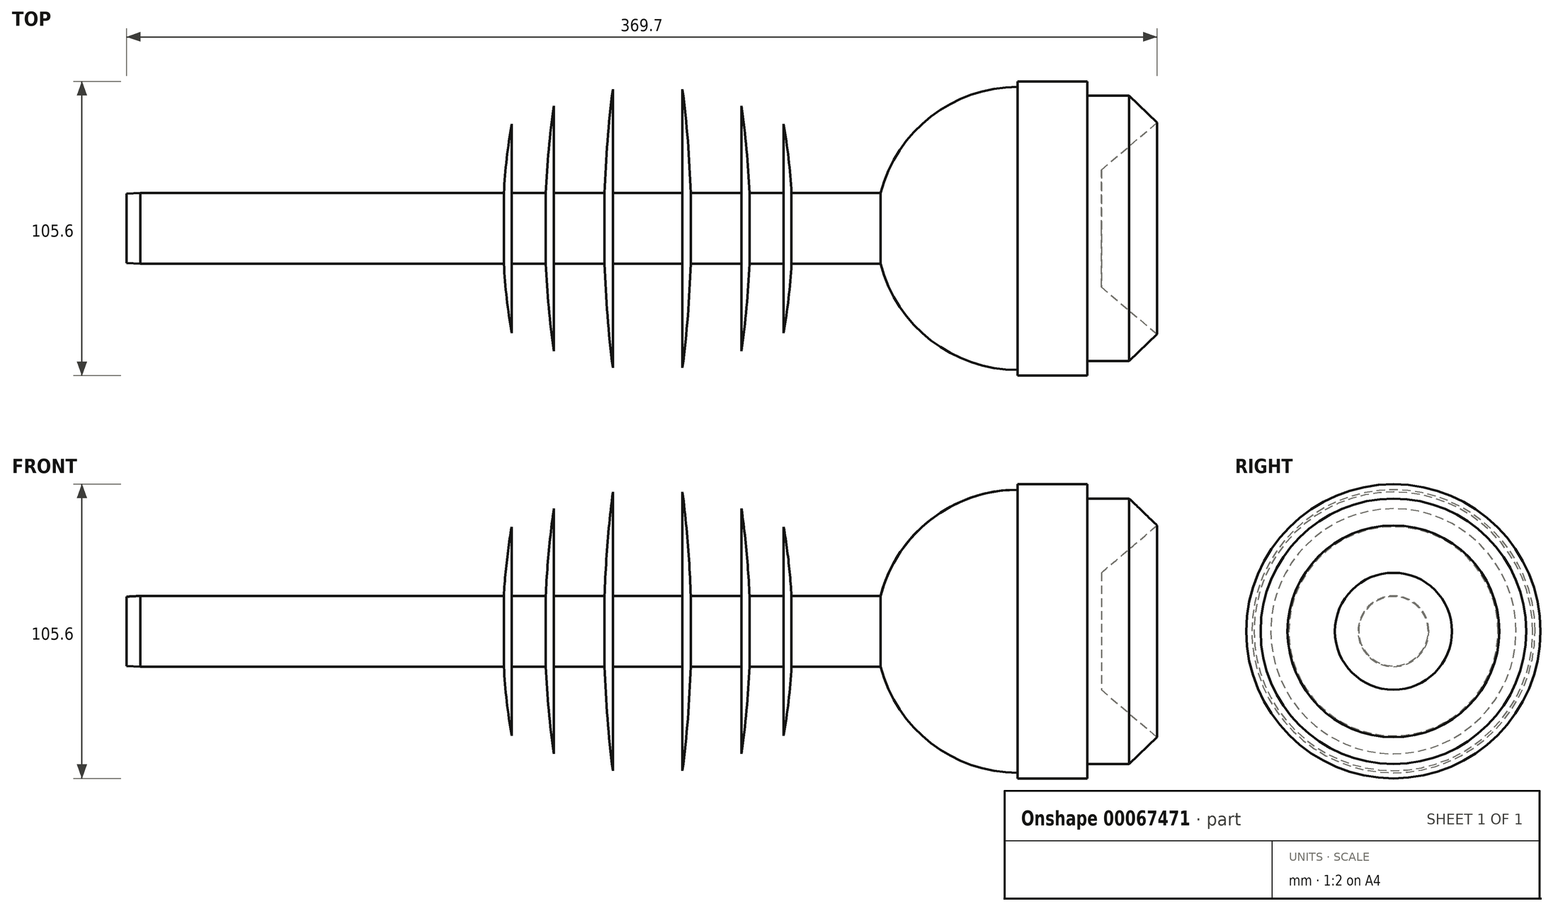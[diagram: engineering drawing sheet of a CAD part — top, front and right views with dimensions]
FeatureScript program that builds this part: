
annotation { "Feature Type Name" : "Feature", "Feature Type Description" : "" }
export const myFeature = defineFeature(function(context is Context, id is Id, definition is map)
    precondition{}
    {
        {
            assignVariable(context, id + "F0", {"name" : "s", "anyValue" : 1});
        }
        {
            var Q0;
            Q0=qCreatedBy(makeId("Top.planeOp"),FACE);
            var sketch = newSketch(context, id + "F1", { "sketchPlane" : qUnion([Q0])});
            skLineSegment(sketch, "E0", {"start": v(0, 0) * mm, "end": v(0, 12.7) * mm});
            skLineSegment(sketch, "E1", {"start": v(0, 12.7) * mm, "end": v(181.95, 12.7) * mm});
            skLineSegment(sketch, "E2", {"start": v(0, 0) * mm, "end": v(130, 0) * mm});
            skLineSegment(sketch, "E3", {"start": v(130, 0) * mm, "end": v(133.15, 0) * mm});
            skLineSegment(sketch, "E4", {"start": v(133.15, 0) * mm, "end": v(145.15, 0) * mm});
            skLineSegment(sketch, "E5", {"start": v(145.15, 0) * mm, "end": v(148.3, 0) * mm});
            skLineSegment(sketch, "E6", {"start": v(148.3, 0) * mm, "end": v(166.3, 0) * mm});
            skLineSegment(sketch, "E7", {"start": v(166.3, 0) * mm, "end": v(169.45, 0) * mm});
            skLineSegment(sketch, "E8", {"start": v(169.45, 0) * mm, "end": v(181.95, 0) * mm});
            skLineSegment(sketch, "E9", {"start": v(130, 0) * mm, "end": v(130, 12.7) * mm, "construction": true});
            skLineSegment(sketch, "E10", {"start": v(145.15, 0) * mm, "end": v(145.15, 12.7) * mm, "construction": true});
            skLineSegment(sketch, "E11", {"start": v(166.3, 0) * mm, "end": v(166.3, 12.7) * mm, "construction": true});
            skLineSegment(sketch, "E12", {"start": v(181.95, 0) * mm, "end": v(181.95, 12.7) * mm, "construction": true});
            skLineSegment(sketch, "E13", {"start": v(133.15, 12.7) * mm, "end": v(133.15, 37.5) * mm});
            skLineSegment(sketch, "E14", {"start": v(148.3, 12.7) * mm, "end": v(148.3, 44) * mm});
            skLineSegment(sketch, "E15", {"start": v(169.45, 12.7) * mm, "end": v(169.45, 50) * mm});
            skArc(sketch, "E16", {"start": v(133.15, 37.5) * mm, "mid": v(130.79, 18.82) * mm, "end": v(130, 0) * mm});
            skArc(sketch, "E17", {"start": v(148.3, 44) * mm, "mid": v(145.94, 22.06) * mm, "end": v(145.15, 0) * mm});
            skArc(sketch, "E18", {"start": v(169.45, 50) * mm, "mid": v(167.09, 25.05) * mm, "end": v(166.3, 0) * mm});
            skLineSegment(sketch, "E19.MirrorCS", {"start": v(194.45, 12.7) * mm, "end": v(194.45, 50) * mm});
            skArc(sketch, "E20.MirrorCS", {"start": v(194.45, 50) * mm, "mid": v(196.81, 25.05) * mm, "end": v(197.6, 0) * mm});
            skLineSegment(sketch, "E21.MirrorCS", {"start": v(215.6, 12.7) * mm, "end": v(215.6, 44) * mm});
            skArc(sketch, "E22.MirrorCS", {"start": v(215.6, 44) * mm, "mid": v(217.96, 22.06) * mm, "end": v(218.75, 0) * mm});
            skLineSegment(sketch, "E23.MirrorCS", {"start": v(230.75, 12.7) * mm, "end": v(230.75, 37.5) * mm});
            skArc(sketch, "E24.MirrorCS", {"start": v(230.75, 37.5) * mm, "mid": v(233.11, 18.82) * mm, "end": v(233.9, 0) * mm});
            skLineSegment(sketch, "E25", {"start": v(181.95, 0) * mm, "end": v(263.9, 0) * mm});
            skLineSegment(sketch, "E26", {"start": v(263.9, 0) * mm, "end": v(314.7, 0) * mm});
            skLineSegment(sketch, "E27", {"start": v(314.7, 0) * mm, "end": v(344.7, 0) * mm});
            skLineSegment(sketch, "E28", {"start": v(344.7, 0) * mm, "end": v(344.7, 21) * mm});
            skLineSegment(sketch, "E29", {"start": v(344.7, 21) * mm, "end": v(364.7, 38) * mm});
            skLineSegment(sketch, "E30", {"start": v(364.7, 38) * mm, "end": v(354.7, 47.65) * mm});
            skLineSegment(sketch, "E31", {"start": v(354.7, 47.65) * mm, "end": v(339.7, 47.65) * mm});
            skLineSegment(sketch, "E32", {"start": v(339.7, 47.65) * mm, "end": v(339.7, 52.8) * mm});
            skLineSegment(sketch, "E33", {"start": v(339.7, 52.8) * mm, "end": v(314.7, 52.8) * mm});
            skLineSegment(sketch, "E34", {"start": v(314.7, 52.8) * mm, "end": v(314.7, 50.8) * mm});
            skLineSegment(sketch, "E35", {"start": v(181.95, 12.7) * mm, "end": v(265.51, 12.7) * mm});
            skArc(sketch, "E36", {"start": v(314.7, 50.8) * mm, "mid": v(283.6, 40.16) * mm, "end": v(265.51, 12.7) * mm});
            skLineSegment(sketch, "E37", {"start": v(314.7, 50.8) * mm, "end": v(314.7, 0) * mm, "construction": true});
            skSolve(sketch);
        }
        {
            var Q0;
            Q0 = qSketchRegion(id + "F1", true);
            var Q1;
            Q1=sQuery(id+"F1.wireOp",EDGE,"E2");
            revolve(context, id + "F2", {"entities" : qUnion([Q0]), "axis" : qUnion([Q1]), "revolveType" : RevolveType.FULL});
        }
        {
            var Q0;
            Q0=makeQuery(id+"F2.opRevolve","SWEPT_FACE",FACE,{"disambiguationData":[OSD([sQuery(id+"F1.wireOp",EDGE,"E0")])]});
            extrude(context, id + "F3", {"entities" : qUnion([Q0]), "operationType" : NewBodyOperationType.ADD, "depth" : (5 * getVariable(context, 's')) * mm, "hasDraft" : true, "draftAngle" : 3 * degree, "draftPullDirection" : true});
        }
        {
            assignVariable(context, id + "F4", {"name" : "scale", "anyValue" : 1});
        }
        {
            var Q0;
            Q0=makeQuery(id+"F2.opRevolve","SWEPT_BODY",BODY,{"disambiguationData":[OSD([sQuery(id+"F1.wireOp",EDGE,"E0"),sQuery(id+"F1.wireOp",EDGE,"E1"),sQuery(id+"F1.wireOp",EDGE,"E2"),sQuery(id+"F1.wireOp",EDGE,"E3"),sQuery(id+"F1.wireOp",EDGE,"E4"),sQuery(id+"F1.wireOp",EDGE,"E5"),sQuery(id+"F1.wireOp",EDGE,"E6"),sQuery(id+"F1.wireOp",EDGE,"E7"),sQuery(id+"F1.wireOp",EDGE,"E8"),sQuery(id+"F1.wireOp",EDGE,"E13"),sQuery(id+"F1.wireOp",EDGE,"E14"),sQuery(id+"F1.wireOp",EDGE,"E15"),sQuery(id+"F1.wireOp",EDGE,"E16"),sQuery(id+"F1.wireOp",EDGE,"E17"),sQuery(id+"F1.wireOp",EDGE,"E18"),sQuery(id+"F1.wireOp",EDGE,"E19.MirrorCS"),sQuery(id+"F1.wireOp",EDGE,"E20.MirrorCS"),sQuery(id+"F1.wireOp",EDGE,"E21.MirrorCS"),sQuery(id+"F1.wireOp",EDGE,"E22.MirrorCS"),sQuery(id+"F1.wireOp",EDGE,"E23.MirrorCS"),sQuery(id+"F1.wireOp",EDGE,"E24.MirrorCS"),sQuery(id+"F1.wireOp",EDGE,"E25"),sQuery(id+"F1.wireOp",EDGE,"E26"),sQuery(id+"F1.wireOp",EDGE,"E27"),sQuery(id+"F1.wireOp",EDGE,"E28"),sQuery(id+"F1.wireOp",EDGE,"E29"),sQuery(id+"F1.wireOp",EDGE,"E30"),sQuery(id+"F1.wireOp",EDGE,"E31"),sQuery(id+"F1.wireOp",EDGE,"E32"),sQuery(id+"F1.wireOp",EDGE,"E33"),sQuery(id+"F1.wireOp",EDGE,"E34"),sQuery(id+"F1.wireOp",EDGE,"E35"),sQuery(id+"F1.wireOp",EDGE,"E36")])]});
            var Q1;
            Q1=qCreatedBy(makeId("Origin.pointOp"),VERTEX);
            transform(context, id + "F5", {"entities" : qUnion([Q0]), "transformType" : TransformType.SCALE_UNIFORMLY, "scale" : getVariable(context, 'scale'), "scalePoint" : qUnion([Q1]), "makeCopy" : false});
        }
    });
